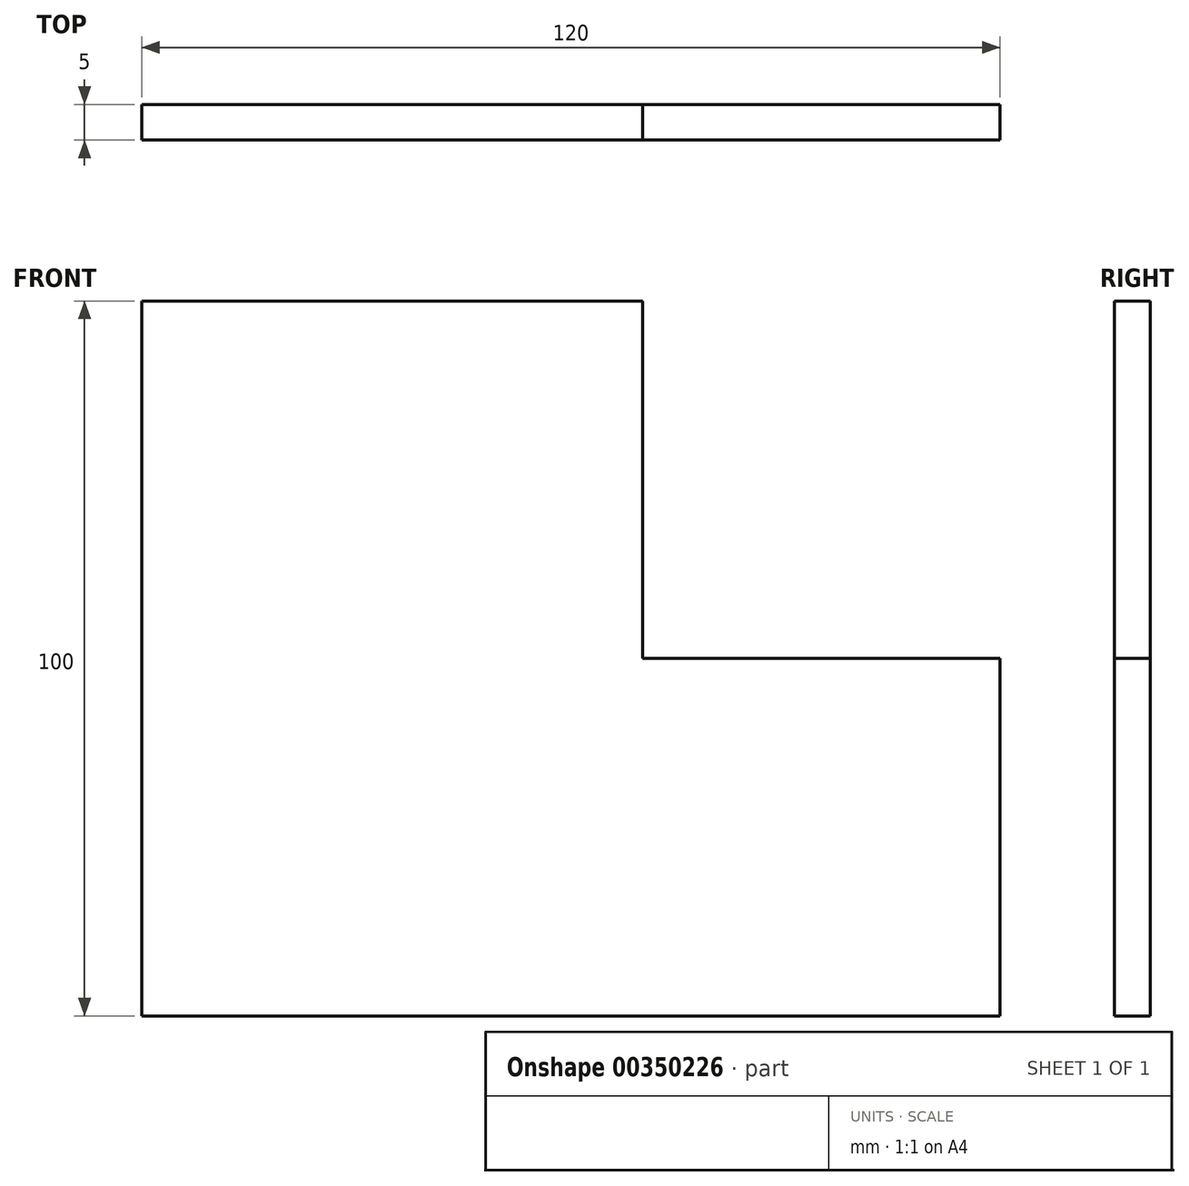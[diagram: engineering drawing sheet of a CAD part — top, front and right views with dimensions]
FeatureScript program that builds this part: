
annotation { "Feature Type Name" : "Feature", "Feature Type Description" : "" }
export const myFeature = defineFeature(function(context is Context, id is Id, definition is map)
    precondition{}
    {
        {
            var Q0;
            Q0=qCreatedBy(makeId("Front.planeOp"),FACE);
            var sketch = newSketch(context, id + "F0", { "sketchPlane" : qUnion([Q0])});
            skLineSegment(sketch, "E0", {"start": v(-77.54, 31.74) * mm, "end": v(-7.54, 31.74) * mm});
            skLineSegment(sketch, "E1", {"start": v(-7.54, 31.74) * mm, "end": v(-7.54, -18.26) * mm});
            skLineSegment(sketch, "E2", {"start": v(-7.54, -18.26) * mm, "end": v(42.46, -18.26) * mm});
            skLineSegment(sketch, "E3", {"start": v(42.46, -18.26) * mm, "end": v(42.46, -68.26) * mm});
            skLineSegment(sketch, "E4", {"start": v(42.46, -68.26) * mm, "end": v(-77.54, -68.26) * mm});
            skLineSegment(sketch, "E5", {"start": v(-77.54, 31.74) * mm, "end": v(-77.54, -68.26) * mm});
            skSolve(sketch);
        }
        {
            var Q0;
            Q0=makeQuery(id+"F0.imprint","IMPRINT",FACE,{"disambiguationData":[TD([[makeQuery(id+"F0.imprint","IMPRINT",EDGE,{"derivedFrom":sQuery(id+"F0.wireOp",EDGE,"E0")}),-1.0]])]});
            extrude(context, id + "F1", {"entities" : qUnion([Q0]), "depth" : 5 * mm});
        }
    });
